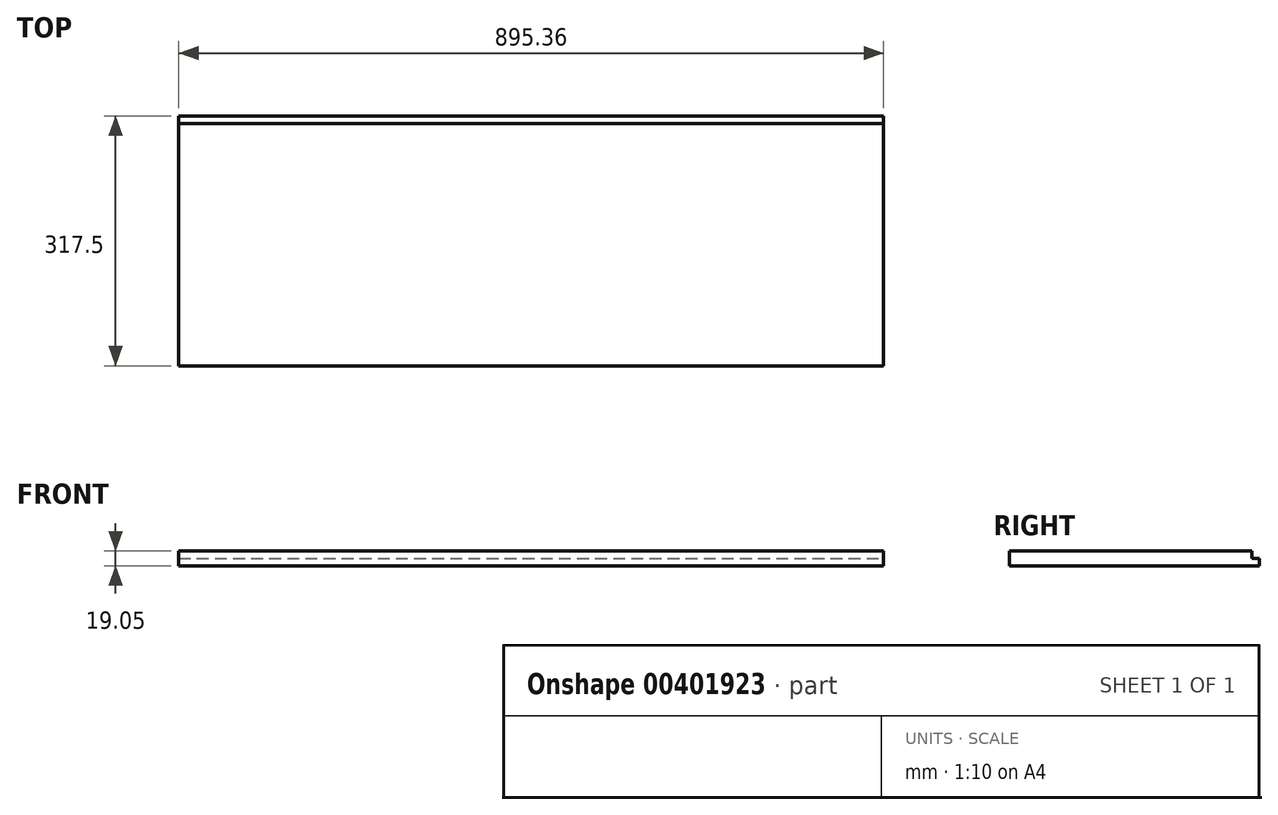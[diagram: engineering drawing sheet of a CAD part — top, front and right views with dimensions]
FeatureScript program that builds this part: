
annotation { "Feature Type Name" : "Feature", "Feature Type Description" : "" }
export const myFeature = defineFeature(function(context is Context, id is Id, definition is map)
    precondition{}
    {
        {
            var Q0;
            Q0=qCreatedBy(makeId("Top.planeOp"),FACE);
            var sketch = newSketch(context, id + "F0", { "sketchPlane" : qUnion([Q0])});
            skLineSegment(sketch, "E0.bottom", {"start": v(447.68, -158.75) * mm, "end": v(-447.68, -158.75) * mm});
            skLineSegment(sketch, "E0.top", {"start": v(447.68, 158.75) * mm, "end": v(-447.68, 158.75) * mm});
            skLineSegment(sketch, "E0.left", {"start": v(447.68, -158.75) * mm, "end": v(447.68, 158.75) * mm});
            skLineSegment(sketch, "E0.right", {"start": v(-447.68, -158.75) * mm, "end": v(-447.68, 158.75) * mm});
            skPoint(sketch, "E0.middle", {"position": v(0, 0) * mm});
            skSolve(sketch);
        }
        {
            var Q0;
            Q0=qSketchRegion(id+"F0",true);
            extrude(context, id + "F1", {"entities" : qUnion([Q0]), "depth" : 19.05 * mm});
        }
        {
            var Q0;
            Q0=makeQuery(id+"F1.opExtrude","SWEPT_FACE",FACE,{"disambiguationData":[OSD([sQuery(id+"F0.wireOp",EDGE,"E0.left")])]});
            var sketch = newSketch(context, id + "F2", { "sketchPlane" : qUnion([Q0])});
            skLineSegment(sketch, "E1.bottom", {"start": v(149.23, 19.05) * mm, "end": v(158.75, 19.05) * mm});
            skLineSegment(sketch, "E1.top", {"start": v(149.23, 9.52) * mm, "end": v(158.75, 9.52) * mm});
            skLineSegment(sketch, "E1.left", {"start": v(149.23, 19.05) * mm, "end": v(149.23, 9.52) * mm});
            skLineSegment(sketch, "E1.right", {"start": v(158.75, 19.05) * mm, "end": v(158.75, 9.52) * mm});
            skSolve(sketch);
        }
        {
            var Q0;
            Q0=qSketchRegion(id+"F2",true);
            extrude(context, id + "F3", {"entities" : qUnion([Q0]), "operationType" : NewBodyOperationType.REMOVE, "endBound" : BoundingType.THROUGH_ALL, "oppositeDirection" : true, "depth" : 25.4 * mm});
        }
    });
